# Revit family: 400_ISR_TTN_multifunctioneel_opbouwarmatuur
name_source: partatom
category: Lighting Fixtures
revit_build: Autodesk Revit 2013 (Build: 20121003_2115(x64)
units: mm (PartAtom-declared; Revit-internal decimal feet)

## types (1)
- 400_ISR_TTN_multifunctioneel_opbouwarmatuur
    Apparent Load = 0 VA
    Color Filter = 16777215
    Description = TTN
    Dimming Lamp Color Temperature Shift = <None>
    Emit Shape Visible in Rendering = No
    Emit from Circle Diameter = 610 mm
    Lamp = TC-S, TC-L, LED
    Load Classification = Other
    Manufacturer = Lightronics
    Model = LOD400
    Photometric Web File = TTN-LLM4-2-12-350-D-OL-1192-230-X-ZL.ies
    Tilt Angle = 90.00°
    URL = http://www.lightronics.nl
    Wattage Comments = TC-S 1 of 2 x 7 Watt, TC-S 1 of 2 x 9 Watt, TC-S 1 of 2 x 11 Watt,TC-L 1 of 2 x 18 Watt, LED 6,9 Watt, LED 12 Watt
    bolle_kap = No
    platte_kap = Yes

## geometry (parser evidence)
native form markers: Sweep x1
no freeform markers — native parametric forms only
